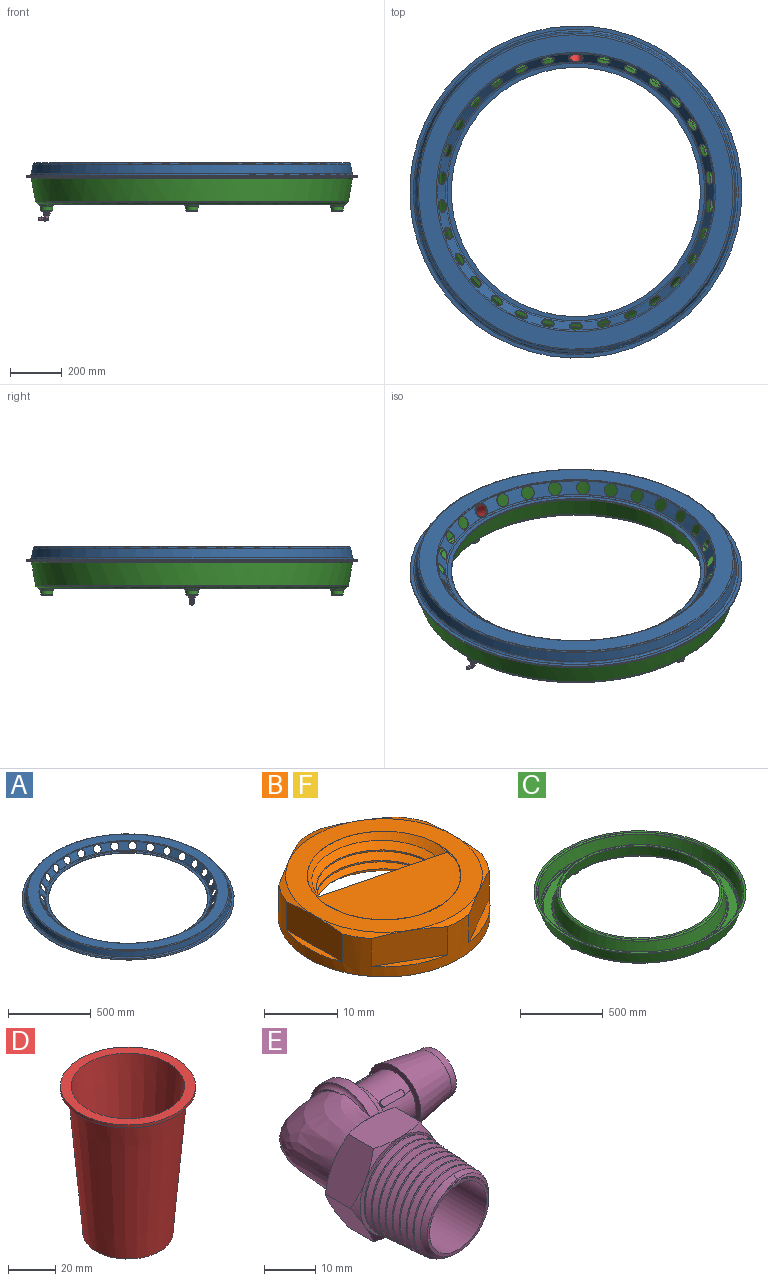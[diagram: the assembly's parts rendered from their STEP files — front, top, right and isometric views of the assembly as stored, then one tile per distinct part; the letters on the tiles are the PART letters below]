
ASSEMBLY  parts=6 mates=7
PART A: 52 faces, bbox 1370.9x1370.9x52.1 mm
  f0: cone r=500.53mm half-angle=35deg, axis (0,0,1), area 110077.8mm2, adj f11,f12,f22,f23,f24,f25,f26,f27
  f1: cone r=502.17mm half-angle=35deg, axis (0,0,1), area 110826.6mm2, adj f19,f20,f22,f23,f24,f25,f26,f27
  f2: plane 964x964mm, normal (0,0,-1), area 6044.4mm2, adj f4,f15
  f3: plane 992.73x992.73mm, normal (0,0,1), area 50195.3mm2, adj f4,f12
  f4: cylinder r=480mm len=960mm, axis (0,0,1), area 9047.8mm2, adj f2,f3
  f5: plane 1280x1280mm, normal (0,0,-1), area 54958.5mm2, adj f6,f21
  f6: cylinder r=640mm len=1280mm, axis (0,0,1), area 8042.5mm2, adj f5,f7
  f7: plane 1280x1280mm, normal (0,0,1), area 54958.5mm2, adj f6,f13
  f8: cone r=610.8mm half-angle=10deg, axis (0,0,-1), area 147454.2mm2, adj f10,f13
  f9: plane 1211.54x1211.54mm, normal (0,0,1), area 243289.2mm2, adj f10,f11
  f10: torus R=605.77mm, axis (0,0,1), area 32073.4mm2, adj f8,f9
  f11: torus R=538.07mm, axis (0,0,1), area 19375.4mm2, adj f0,f9
  f12: torus R=496.36mm, axis (0,0,-1), area 24121.8mm2, adj f0,f3
  f13: torus R=626.18mm, axis (0,0,1), area 43615.7mm2, adj f7,f8
  f14: plane 992.73x992.73mm, normal (0,0,-1), area 44150.9mm2, adj f15,f20
  f15: cylinder r=482mm len=964mm, axis (0,0,1), area 3028.5mm2, adj f2,f14
  f16: cone r=608.84mm half-angle=10deg, axis (0,0,-1), area 146981.9mm2, adj f18,f21
  f17: plane 1211.54x1211.54mm, normal (0,0,-1), area 243289.2mm2, adj f18,f19
  f18: torus R=605.77mm, axis (0,0,1), area 21340.7mm2, adj f16,f17
  f19: torus R=538.07mm, axis (0,0,1), area 12938.4mm2, adj f1,f17
  f20: torus R=496.36mm, axis (0,0,-1), area 30205.8mm2, adj f1,f14
  f21: torus R=626.18mm, axis (0,0,1), area 54415.8mm2, adj f5,f16
  f22: cylinder r=25.5mm len=48.92mm, axis (0.33,0.75,0.57), area 320.5mm2, adj f0,f1
  f23: cylinder r=25.5mm len=47.56mm, axis (0.71,0.41,0.57), area 320.6mm2, adj f0,f1
  f24: cylinder r=25.5mm len=44.03mm, axis (0.61,0.55,0.57), area 320.5mm2, adj f0,f1
  f25: cylinder r=25.5mm len=45.91mm, axis (0.48,0.66,0.57), area 320.5mm2, adj f0,f1
  f26: cylinder r=25.5mm len=49.98mm, axis (0.78,-0.25,0.57), area 320.4mm2, adj f0,f1
  f27: cylinder r=25.5mm len=49.98mm, axis (0.78,0.25,0.57), area 320.6mm2, adj f0,f1
  f28: cylinder r=25.5mm len=51.03mm, axis (0.81,0.09,0.57), area 320.5mm2, adj f0,f1
  f29: cylinder r=25.5mm len=51.03mm, axis (0.81,-0.09,0.57), area 320.6mm2, adj f0,f1
  f30: cylinder r=25.5mm len=51mm, axis (0,-0.82,0.57), area 320.6mm2, adj f0,f1
  f31: cylinder r=25.5mm len=47.56mm, axis (0.71,-0.41,0.57), area 320.6mm2, adj f0,f1
  f32: cylinder r=25.5mm len=44.03mm, axis (0.61,-0.55,0.57), area 320.5mm2, adj f0,f1
  f33: cylinder r=25.5mm len=45.91mm, axis (0.48,-0.66,0.57), area 320.6mm2, adj f0,f1
  f34: cylinder r=25.5mm len=48.92mm, axis (0.33,-0.75,0.57), area 320.6mm2, adj f0,f1
  f35: cylinder r=25.5mm len=50.68mm, axis (0.17,-0.8,0.57), area 320.6mm2, adj f0,f1
  f36: cylinder r=25.5mm len=50.68mm, axis (-0.17,-0.8,0.57), area 320.6mm2, adj f0,f1
  f37: cylinder r=25.5mm len=48.92mm, axis (-0.33,-0.75,0.57), area 320.6mm2, adj f0,f1
  f38: cylinder r=25.5mm len=45.91mm, axis (-0.48,-0.66,0.57), area 320.6mm2, adj f0,f1
  f39: cylinder r=25.5mm len=44.03mm, axis (-0.61,-0.55,0.57), area 320.6mm2, adj f0,f1
  f40: cylinder r=25.5mm len=47.56mm, axis (-0.71,-0.41,0.57), area 320.5mm2, adj f0,f1
  f41: cylinder r=25.5mm len=49.98mm, axis (-0.78,-0.25,0.57), area 320.6mm2, adj f0,f1
  f42: cylinder r=25.5mm len=51.03mm, axis (-0.81,-0.09,0.57), area 320.6mm2, adj f0,f1
  f43: cylinder r=25.5mm len=51.03mm, axis (-0.81,0.09,0.57), area 320.6mm2, adj f0,f1
  f44: cylinder r=25.5mm len=49.98mm, axis (-0.78,0.25,0.57), area 320.5mm2, adj f0,f1
  f45: cylinder r=25.5mm len=47.56mm, axis (-0.71,0.41,0.57), area 320.5mm2, adj f0,f1
  f46: cylinder r=25.5mm len=44.03mm, axis (-0.61,0.55,0.57), area 320.5mm2, adj f0,f1
  f47: cylinder r=25.5mm len=45.91mm, axis (-0.48,0.66,0.57), area 320.6mm2, adj f0,f1
  f48: cylinder r=25.5mm len=48.92mm, axis (-0.33,0.75,0.57), area 320.5mm2, adj f0,f1
  f49: cylinder r=25.5mm len=50.68mm, axis (-0.17,0.8,0.57), area 320.5mm2, adj f0,f1
  f50: cylinder r=25.5mm len=51mm, axis (0,0.82,0.57), area 320.6mm2, adj f0,f1
  f51: cylinder r=25.5mm len=50.68mm, axis (0.17,0.8,0.57), area 320.5mm2, adj f0,f1
PART B: 31 faces, bbox 29.5x29.5x11.2 mm
  f0: cone r=10.46mm half-angle=45deg, axis (0,0,1), area 62.4mm2, adj f1,f26,f27,f28,f29,f30
  f1: bspline ~21.52x21.42mm, area 287.5mm2, adj f0,f2,f25,f26
  f2: cone r=10.67mm half-angle=1.8deg, axis (0,0,-1), area 22.2mm2, adj f1,f3,f27,f28
  f3: plane 29.04x29.04mm, normal (0,0,-1), area 299.6mm2, adj f2,f4,f5,f6
  f4: bspline ~5.86x2.79mm, area 0mm2, adj f3,f5,f25
  f5: bspline ~21.61x21.56mm, area 1.4mm2, adj f3,f4,f25
  f6: cylinder r=14.48mm len=28.95mm, axis (0,0,1), area 268.5mm2, adj f3,f7,f8,f9,f10,f11,f12,f13
  f7: cone r=13.44mm half-angle=70deg, axis (0,0,-1), area 10.2mm2, adj f6,f9,f23,f28
  f8: plane 9.33x5.39mm, normal (0,0,1), area 7.5mm2, adj f6,f9
  f9: plane 9.9x5.95mm, normal (0.5,0.87,0), area 53mm2, adj f6,f7,f8,f10
  f10: cone r=13.44mm half-angle=70deg, axis (0,0,-1), area 10.2mm2, adj f6,f9,f12,f28
  f11: plane 9.33x5.39mm, normal (0,0,1), area 7.5mm2, adj f6,f12
  f12: plane 9.9x5.95mm, normal (-0.5,0.87,0), area 53mm2, adj f6,f10,f11,f13
  f13: cone r=13.44mm half-angle=70deg, axis (0,0,-1), area 10.2mm2, adj f6,f12,f15,f28
  f14: plane 10.77x1.04mm, normal (0,0,1), area 7.5mm2, adj f6,f15
  f15: plane 11.34x5.61mm, normal (-1,0,0), area 53mm2, adj f6,f13,f14,f16
  f16: cone r=13.44mm half-angle=70deg, axis (0,0,-1), area 10.2mm2, adj f6,f15,f18,f28
  f17: plane 9.33x5.39mm, normal (0,0,1), area 7.5mm2, adj f6,f18
  f18: plane 9.9x5.95mm, normal (-0.5,-0.87,0), area 53mm2, adj f6,f16,f17,f19
  f19: cone r=13.44mm half-angle=70deg, axis (0,0,-1), area 10.2mm2, adj f6,f18,f21,f28
  f20: plane 9.33x5.39mm, normal (0,0,1), area 7.5mm2, adj f6,f21
  f21: plane 9.9x5.95mm, normal (0.5,-0.87,0), area 53mm2, adj f6,f19,f20,f22
  f22: cone r=13.44mm half-angle=70deg, axis (0,0,-1), area 10.2mm2, adj f6,f21,f23,f28
  f23: plane 11.34x5.61mm, normal (1,0,0), area 53mm2, adj f6,f7,f22,f24
  f24: plane 10.77x1.04mm, normal (0,0,1), area 7.5mm2, adj f6,f23
  f25: cone r=10.67mm half-angle=45deg, axis (0,0,-1), area 67mm2, adj f1,f4,f5,f26,f27
  f26: bspline ~18.55x18.5mm, area 30mm2, adj f0,f1,f25,f27
  f27: bspline ~21.26x21.16mm, area 157.2mm2, adj f0,f2,f25,f26
  f28: plane 26.96x26.96mm, normal (0,0,1), area 222.2mm2, adj f0,f2,f7,f10,f13,f16,f19,f22
  f29: bspline ~21.21x21.17mm, area 52.7mm2, adj f0,f28,f30
  f30: bspline ~5.58x3.69mm, area 0mm2, adj f0,f28,f29
PART C: 94 faces, bbox 1370.9x1370.9x134 mm
  f0: plane 987.63x987.63mm, normal (0,0,1), area 42268.3mm2, adj f5,f60
  f1: plane 573.4x573.4mm, normal (0,0,-1), area 43918mm2, adj f15,f16,f29,f41
  f2: plane 573.4x573.4mm, normal (0,0,-1), area 43918mm2, adj f15,f16,f30,f33
  f3: plane 573.4x573.4mm, normal (0,0,-1), area 43918mm2, adj f15,f16,f37,f42
  f4: plane 1280x1280mm, normal (0,0,1), area 54958.5mm2, adj f13,f61
  f5: cylinder r=480mm len=960mm, axis (0,0,1), area 6031.9mm2, adj f0,f6
  f6: plane 987.63x987.63mm, normal (0,0,-1), area 42268.3mm2, adj f5,f18
  f7: cone r=517.63mm half-angle=10deg, axis (0,0,-1), area 281753.6mm2, adj f14,f18
  f8: cone r=517.63mm half-angle=51deg, axis (0,0,-1), area 28389mm2, adj f14,f15
  f9: plane 573.4x573.4mm, normal (0,0,-1), area 43918mm2, adj f15,f16,f34,f38
  f10: cone r=590mm half-angle=51deg, axis (0,0,1), area 32301.8mm2, adj f16,f17
  f11: cone r=619.47mm half-angle=10deg, axis (0,0,1), area 337802.8mm2, adj f17,f19
  f12: plane 1280x1280mm, normal (0,0,-1), area 54958.5mm2, adj f13,f19
  f13: cylinder r=640mm len=1280mm, axis (0,0,1), area 8042.5mm2, adj f4,f12
  f14: torus R=526.83mm, axis (0,0,-1), area 23331.7mm2, adj f7,f8
  f15: torus R=533.54mm, axis (0,0,1), area 22508mm2, adj f1,f2,f3,f8,f9,f31,f35,f36
  f16: torus R=586.46mm, axis (0,0,1), area 25041.4mm2, adj f1,f2,f3,f9,f10,f28,f32,f39
  f17: torus R=593.17mm, axis (0,0,-1), area 27076.3mm2, adj f10,f11
  f18: torus R=493.82mm, axis (0,0,-1), area 34990.2mm2, adj f6,f7
  f19: torus R=626.18mm, axis (0,0,-1), area 43615.7mm2, adj f11,f12
  f20: cone r=25mm half-angle=5deg, axis (0,0,1), area 2401.2mm2, adj f40,f41,f42,f43,f47
  f21: plane 36.46x36.46mm, normal (0,0,-1), area 656.2mm2, adj f47,f93
  f22: cone r=25mm half-angle=5deg, axis (0,0,1), area 2401.2mm2, adj f36,f37,f38,f39,f46
  f23: plane 36.46x36.46mm, normal (0,0,-1), area 656.2mm2, adj f46,f92
  f24: cone r=25mm half-angle=5deg, axis (0,0,1), area 2401.2mm2, adj f32,f33,f34,f35,f45
  f25: plane 36.46x36.46mm, normal (0,0,-1), area 656.2mm2, adj f45,f91
  f26: cone r=25mm half-angle=5deg, axis (0,0,1), area 2401.2mm2, adj f28,f29,f30,f31,f44
  f27: plane 36.46x36.46mm, normal (0,0,-1), area 656.2mm2, adj f44,f90
  f28: bspline ~31.5x7.73mm, area 167.7mm2, adj f16,f26,f29,f30
  f29: torus R=29.58mm, axis (0,0,1), area 435.5mm2, adj f1,f26,f28,f31
  f30: torus R=29.58mm, axis (0,0,1), area 435.5mm2, adj f2,f26,f28,f31
  f31: bspline ~30.27x7.43mm, area 159.4mm2, adj f15,f26,f29,f30
  f32: bspline ~31.5x7.73mm, area 167.7mm2, adj f16,f24,f33,f34
  f33: torus R=29.58mm, axis (0,0,1), area 435.5mm2, adj f2,f24,f32,f35
  f34: torus R=29.58mm, axis (0,0,1), area 435.5mm2, adj f9,f24,f32,f35
  f35: bspline ~30.27x7.43mm, area 159.4mm2, adj f15,f24,f33,f34
  f36: bspline ~30.27x7.43mm, area 159.4mm2, adj f15,f22,f37,f38
  f37: torus R=29.58mm, axis (0,0,1), area 435.5mm2, adj f3,f22,f36,f39
  f38: torus R=29.58mm, axis (0,0,1), area 435.5mm2, adj f9,f22,f36,f39
  f39: bspline ~31.5x7.73mm, area 167.7mm2, adj f16,f22,f37,f38
  f40: bspline ~30.27x7.43mm, area 159.4mm2, adj f15,f20,f41,f42
  f41: torus R=29.58mm, axis (0,0,1), area 435.5mm2, adj f1,f20,f40,f43
  f42: torus R=29.58mm, axis (0,0,1), area 435.5mm2, adj f3,f20,f40,f43
  f43: bspline ~31.5x7.73mm, area 167.7mm2, adj f16,f20,f41,f42
  f44: torus R=18.23mm, axis (0,0,-1), area 993.1mm2, adj f26,f27
  f45: torus R=18.23mm, axis (0,0,-1), area 993.1mm2, adj f24,f25
  f46: torus R=18.23mm, axis (0,0,-1), area 993.1mm2, adj f22,f23
  f47: torus R=18.23mm, axis (0,0,-1), area 993.1mm2, adj f20,f21
  f48: plane 573.4x573.4mm, normal (0,0,1), area 43918mm2, adj f57,f58,f71,f83
  f49: plane 573.4x573.4mm, normal (0,0,1), area 43918mm2, adj f57,f58,f72,f75
  f50: plane 573.4x573.4mm, normal (0,0,1), area 43918mm2, adj f57,f58,f79,f84
  f51: cone r=519.6mm half-angle=10deg, axis (0,0,-1), area 282843.2mm2, adj f56,f60
  f52: cone r=518.89mm half-angle=51deg, axis (0,0,-1), area 28457.2mm2, adj f56,f57
  f53: plane 573.4x573.4mm, normal (0,0,1), area 43918mm2, adj f57,f58,f76,f80
  f54: cone r=588.74mm half-angle=51deg, axis (0,0,1), area 32233.6mm2, adj f58,f59
  f55: cone r=617.5mm half-angle=10deg, axis (0,0,1), area 336713.3mm2, adj f59,f61
  f56: torus R=526.83mm, axis (0,0,-1), area 18726mm2, adj f51,f52
  f57: torus R=533.54mm, axis (0,0,1), area 18028.7mm2, adj f48,f49,f50,f52,f53,f73,f77,f78
  f58: torus R=586.46mm, axis (0,0,1), area 20010.8mm2, adj f48,f49,f50,f53,f54,f70,f74,f81
  f59: torus R=593.17mm, axis (0,0,-1), area 21600.3mm2, adj f54,f55
  f60: torus R=493.82mm, axis (0,0,-1), area 43841.6mm2, adj f0,f51
  f61: torus R=626.18mm, axis (0,0,-1), area 54415.8mm2, adj f4,f55
  f62: cone r=23.01mm half-angle=5deg, axis (0,0,1), area 2201.1mm2, adj f82,f83,f84,f85,f89
  f63: plane 36.46x36.46mm, normal (0,0,1), area 656.2mm2, adj f89,f93
  f64: cone r=23.01mm half-angle=5deg, axis (0,0,1), area 2201.1mm2, adj f78,f79,f80,f81,f88
  f65: plane 36.46x36.46mm, normal (0,0,1), area 656.2mm2, adj f88,f92
  f66: cone r=23.01mm half-angle=5deg, axis (0,0,1), area 2201.1mm2, adj f74,f75,f76,f77,f87
  f67: plane 36.46x36.46mm, normal (0,0,1), area 656.2mm2, adj f87,f91
  f68: cone r=23.01mm half-angle=5deg, axis (0,0,1), area 2201.1mm2, adj f70,f71,f72,f73,f86
  f69: plane 36.46x36.46mm, normal (0,0,1), area 656.2mm2, adj f86,f90
  f70: bspline ~31.51x9mm, area 222.6mm2, adj f58,f68,f71,f72
  f71: torus R=29.58mm, axis (0,0,1), area 581.4mm2, adj f48,f68,f70,f73
  f72: torus R=29.58mm, axis (0,0,1), area 581.4mm2, adj f49,f68,f70,f73
  f73: bspline ~30.26x8.72mm, area 211.6mm2, adj f57,f68,f71,f72
  f74: bspline ~31.51x9mm, area 222.6mm2, adj f58,f66,f75,f76
  f75: torus R=29.58mm, axis (0,0,1), area 581.4mm2, adj f49,f66,f74,f77
  f76: torus R=29.58mm, axis (0,0,1), area 581.4mm2, adj f53,f66,f74,f77
  f77: bspline ~30.26x8.72mm, area 211.6mm2, adj f57,f66,f75,f76
  f78: bspline ~30.26x8.72mm, area 211.6mm2, adj f57,f64,f79,f80
  f79: torus R=29.58mm, axis (0,0,1), area 581.4mm2, adj f50,f64,f78,f81
  f80: torus R=29.58mm, axis (0,0,1), area 581.4mm2, adj f53,f64,f78,f81
  f81: bspline ~31.51x9mm, area 222.6mm2, adj f58,f64,f79,f80
  f82: bspline ~30.26x8.72mm, area 211.6mm2, adj f57,f62,f83,f84
  f83: torus R=29.58mm, axis (0,0,1), area 581.4mm2, adj f48,f62,f82,f85
  f84: torus R=29.58mm, axis (0,0,1), area 581.4mm2, adj f50,f62,f82,f85
  f85: bspline ~31.51x9mm, area 222.6mm2, adj f58,f62,f83,f84
  f86: torus R=18.23mm, axis (0,0,-1), area 561.4mm2, adj f68,f69
  f87: torus R=18.23mm, axis (0,0,-1), area 561.4mm2, adj f66,f67
  f88: torus R=18.23mm, axis (0,0,-1), area 561.4mm2, adj f64,f65
  f89: torus R=18.23mm, axis (0,0,-1), area 561.4mm2, adj f62,f63
  f90: cylinder r=11.11mm len=22.23mm, axis (0,0,1), area 139.6mm2, adj f27,f69
  f91: cylinder r=11.11mm len=22.23mm, axis (0,0,1), area 139.6mm2, adj f25,f67
  f92: cylinder r=11.11mm len=22.23mm, axis (0,0,1), area 139.6mm2, adj f23,f65
  f93: cylinder r=11.11mm len=22.23mm, axis (0,0,1), area 139.6mm2, adj f21,f63
PART D: 7 faces, bbox 57.2x57.2x76.2 mm
  f0: plane 38.1x38.1mm, normal (0,0,-1), area 1140.1mm2, adj f1
  f1: cone r=25.4mm half-angle=4.9deg, axis (0,0,1), area 10465.7mm2, adj f0,f2
  f2: plane 57.15x57.15mm, normal (0,0,-1), area 538.4mm2, adj f1,f3
  f3: cylinder r=28.57mm len=57.15mm, axis (0,0,-1), area 273.6mm2, adj f2,f4
  f4: plane 57.15x57.15mm, normal (0,0,1), area 755.6mm2, adj f3,f6
  f5: plane 35.3x35.3mm, normal (0,0,1), area 978.7mm2, adj f6
  f6: cone r=23.88mm half-angle=4.9deg, axis (0,0,1), area 9806.5mm2, adj f4,f5
PART E: 64 faces, bbox 45.4x50.3x26.7 mm
  f0: bspline ~20.25x20.25mm, area 156.1mm2, adj f12,f38
  f1: cylinder r=4.56mm len=31.55mm, axis (1,0,0), area 871.2mm2, adj f2,f39,f63
  f2: cylinder r=4.56mm len=14.71mm, axis (0,-1,0), area 388.8mm2, adj f1,f25,f63
  f3: torus R=9.37mm, axis (-1,0,0), area 58.5mm2, adj f7,f12,f41,f42
  f4: cone r=5.47mm half-angle=9.9deg, axis (-1,0,0), area 410.8mm2, adj f5,f40
  f5: cylinder r=5.47mm len=10.94mm, axis (-1,0,0), area 49.8mm2, adj f4,f39
  f6: torus R=9.37mm, axis (-1,0,0), area 244.9mm2, adj f7,f13
  f7: cylinder r=9.37mm len=18.73mm, axis (-1,0,0), area 126.8mm2, adj f3,f6,f12
  f8: cylinder r=7.81mm len=22.73mm, axis (0,-1,0), area 1114.9mm2, adj f24,f25
  f9: cone r=10.67mm half-angle=45deg, axis (0,1,0), area 50.6mm2, adj f10,f21,f22,f23,f24
  f10: cone r=10.67mm half-angle=45deg, axis (0,1,0), area 9.5mm2, adj f9,f11,f21,f22
  f11: cone r=10.67mm half-angle=3.5deg, axis (0,1,0), area 136.7mm2, adj f10,f20,f21,f22
  f12: bspline ~21.01x19.98mm, area 748.8mm2, adj f0,f3,f7,f41,f42
  f13: cylinder r=5.9mm len=11.8mm, axis (-1,0,0), area 275.8mm2, adj f6,f40,f44,f45,f46,f47,f48,f49
  f14: plane 13.89x9.95mm, normal (0,0,1), area 105.3mm2, adj f15,f19,f26,f27,f33,f37
  f15: plane 12.17x9.94mm, normal (-0.87,0,0.5), area 105.3mm2, adj f14,f16,f26,f28,f36,f37
  f16: plane 12.17x9.94mm, normal (-0.87,0,-0.5), area 105.3mm2, adj f15,f17,f28,f29,f35,f36
  f17: plane 13.89x9.95mm, normal (0,0,-1), area 105.3mm2, adj f16,f18,f29,f30,f34,f35
  f18: plane 12.17x9.94mm, normal (0.87,0,-0.5), area 105.3mm2, adj f17,f19,f30,f31,f32,f34
  f19: plane 12.17x9.94mm, normal (0.87,0,0.5), area 105.3mm2, adj f14,f18,f27,f31,f32,f33
  f20: plane 22.85x22.85mm, normal (0,-1,0), area 65.7mm2, adj f11,f21,f22,f23,f26,f27,f28,f29
  f21: bspline ~21.17x20.81mm, area 687.1mm2, adj f9,f10,f11,f20,f23
  f22: bspline ~22.38x22.24mm, area 843.5mm2, adj f9,f10,f11,f20,f23
  f23: bspline ~19.1x19.04mm, area 112mm2, adj f9,f20,f21,f22
  f24: plane 16.88x16.88mm, normal (0,-1,0), area 32.4mm2, adj f8,f9
  f25: plane 15.61x15.61mm, normal (0,-1,0), area 126.1mm2, adj f2,f8
  f26: cone r=11.11mm half-angle=60deg, axis (0,1,0), area 12.1mm2, adj f14,f15,f20
  f27: cone r=11.11mm half-angle=60deg, axis (0,1,0), area 12.1mm2, adj f14,f19,f20
  f28: cone r=11.11mm half-angle=60deg, axis (0,1,0), area 12.1mm2, adj f15,f16,f20
  f29: cone r=11.11mm half-angle=60deg, axis (0,1,0), area 12.1mm2, adj f16,f17,f20
  f30: cone r=11.11mm half-angle=60deg, axis (0,1,0), area 12.1mm2, adj f17,f18,f20
  f31: cone r=11.11mm half-angle=60deg, axis (0,1,0), area 12.1mm2, adj f18,f19,f20
  f32: cone r=11.11mm half-angle=60deg, axis (0,-1,0), area 12.1mm2, adj f18,f19,f38
  f33: cone r=11.11mm half-angle=60deg, axis (0,-1,0), area 12.1mm2, adj f14,f19,f38
  f34: cone r=11.11mm half-angle=60deg, axis (0,-1,0), area 12.1mm2, adj f17,f18,f38
  f35: cone r=11.11mm half-angle=60deg, axis (0,-1,0), area 12.1mm2, adj f16,f17,f38
  f36: cone r=11.11mm half-angle=60deg, axis (0,-1,0), area 12.1mm2, adj f15,f16,f38
  f37: cone r=11.11mm half-angle=60deg, axis (0,-1,0), area 12.1mm2, adj f14,f15,f38
  f38: plane 22.37x22.37mm, normal (0,1,0), area 69mm2, adj f0,f32,f33,f34,f35,f36,f37
  f39: plane 10.94x10.94mm, normal (1,0,0), area 28.7mm2, adj f1,f5
  f40: plane 14.48x14.48mm, normal (-1,0,0), area 55.3mm2, adj f4,f13
  f41: plane 8.81x8.33mm, normal (-1,0,0), area 2.6mm2, adj f3,f12
  f42: plane 8.81x8.33mm, normal (-1,0,0), area 2.6mm2, adj f3,f12
  f43: plane 6.17x1.02mm, normal (0,0.71,-0.71), area 8.5mm2, adj f44,f45,f46,f47
  f44: plane 4.72x0.21mm, normal (0,0.71,0.71), area 1.4mm2, adj f13,f43,f45,f47
  f45: cylinder r=0.72mm len=1.24mm, axis (0,0.71,-0.71), area 0.7mm2, adj f13,f43,f44,f46
  f46: plane 4.72x0.21mm, normal (0,-0.71,-0.71), area 1.4mm2, adj f13,f43,f45,f47
  f47: cylinder r=0.72mm len=1.24mm, axis (0,0.71,-0.71), area 0.7mm2, adj f13,f43,f44,f46
  f48: cylinder r=0.72mm len=1.24mm, axis (0,0.71,-0.71), area 0.7mm2, adj f13,f49,f51,f52
  f49: plane 4.72x0.21mm, normal (0,-0.71,-0.71), area 1.4mm2, adj f13,f48,f50,f52
  f50: cylinder r=0.72mm len=1.24mm, axis (0,0.71,-0.71), area 0.7mm2, adj f13,f49,f51,f52
  f51: plane 4.72x0.21mm, normal (0,0.71,0.71), area 1.4mm2, adj f13,f48,f50,f52
  f52: plane 6.17x1.02mm, normal (0,-0.71,0.71), area 8.5mm2, adj f48,f49,f50,f51
  f53: plane 6.17x1.02mm, normal (0,-0.71,-0.71), area 8.5mm2, adj f54,f55,f56,f57
  f54: plane 4.72x0.21mm, normal (0,-0.71,0.71), area 1.4mm2, adj f13,f53,f55,f57
  f55: cylinder r=0.72mm len=1.24mm, axis (0,0.71,0.71), area 0.7mm2, adj f13,f53,f54,f56
  f56: plane 4.72x0.21mm, normal (0,0.71,-0.71), area 1.4mm2, adj f13,f53,f55,f57
  f57: cylinder r=0.72mm len=1.24mm, axis (0,0.71,0.71), area 0.7mm2, adj f13,f53,f54,f56
  f58: cylinder r=0.72mm len=1.24mm, axis (0,0.71,0.71), area 0.7mm2, adj f13,f59,f61,f62
  f59: plane 4.72x0.21mm, normal (0,0.71,-0.71), area 1.4mm2, adj f13,f58,f60,f62
  f60: cylinder r=0.72mm len=1.24mm, axis (0,0.71,0.71), area 0.7mm2, adj f13,f59,f61,f62
  f61: plane 4.72x0.21mm, normal (0,-0.71,0.71), area 1.4mm2, adj f13,f58,f60,f62
  f62: plane 6.17x1.02mm, normal (0,0.71,0.71), area 8.5mm2, adj f58,f59,f60,f61
  f63: sphere r=4.56mm, area 65.3mm2, adj f1,f2
PART F: same geometry as B
PLACE A at identity fixed
PLACE B t=(-560,0,-133)mm
PLACE C at identity
PLACE D rot(axis=(1,0,0),55deg) t=(0,579.21,-14.83)mm
PLACE E rot(axis=(-0.02,-0.71,0.71),177.8deg) t=(-560,0,-144.58)mm
PLACE F rot(axis=(1,0,0),180deg) t=(-560,0,-135)mm
MATE planar F.f28 <-> E.f20  axis (0,0,-1) through (-559.99,-0.02,-141.73)mm
MATE planar B.f3 <-> C.f22  axis (0,0,-1) through (-560.02,0,-133)mm
MATE cylindrical F.f0 <-> E.f8  axis (0,0,-1) through (-560,0,-141.35)mm
MATE cylindrical D.f1 <-> A.f30  axis (0,-0.82,0.57) through (0,548.62,6.58)mm
MATE cylindrical B.f0 <-> E.f8  axis (0,0,1) through (-560,0,-129.82)mm
MATE planar F.f3 <-> C.f22  axis (0,0,1) through (-560.02,0,-135)mm
MATE cylindrical E.f8 <-> C.f92  axis (0,0,1) through (-560,0,-125.86)mm
